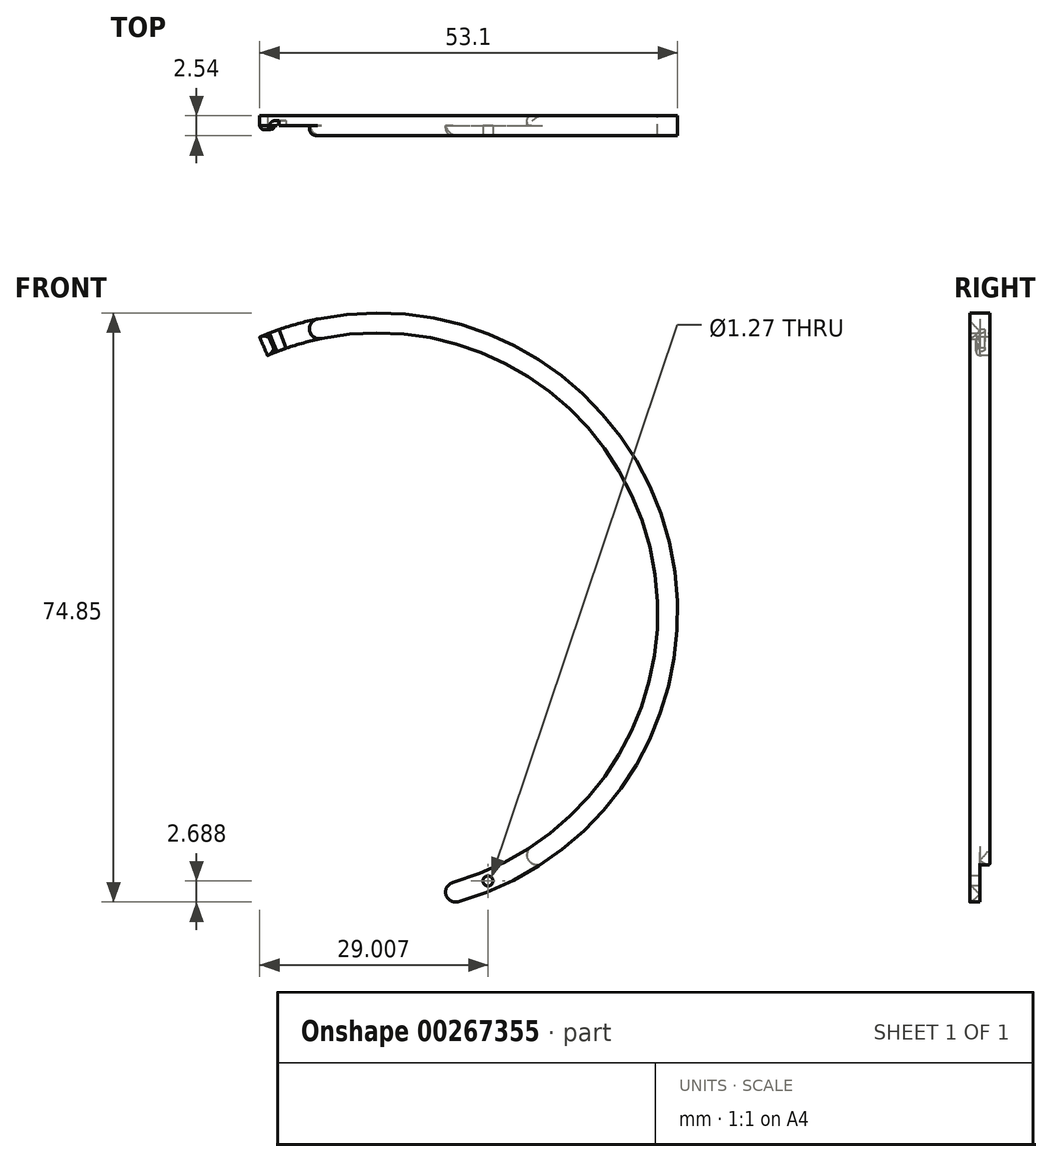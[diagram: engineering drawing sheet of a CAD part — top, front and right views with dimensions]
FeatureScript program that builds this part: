
annotation { "Feature Type Name" : "Feature", "Feature Type Description" : "" }
export const myFeature = defineFeature(function(context is Context, id is Id, definition is map)
    precondition{}
    {
        {
            var Q0;
            Q0=qCreatedBy(makeId("Front.planeOp"),FACE);
            var sketch = newSketch(context, id + "F0", { "sketchPlane" : qUnion([Q0])});
            skArc(sketch, "E0", {"start": v(8.35, -34.57) * mm, "mid": v(34.57, 8.35) * mm, "end": v(-8.35, 34.57) * mm});
            skArc(sketch, "E1", {"start": v(8.95, -37.03) * mm, "mid": v(37.03, 8.95) * mm, "end": v(-8.95, 37.03) * mm});
            skLineSegment(sketch, "E2", {"start": v(-8.95, 37.03) * mm, "end": v(-8.35, 34.57) * mm});
            skLineSegment(sketch, "E3", {"start": v(18.51, -30.36) * mm, "end": v(19.83, -32.53) * mm});
            skLineSegment(sketch, "E4.trimOffspring", {"start": v(8.35, -34.57) * mm, "end": v(8.95, -37.03) * mm});
            skPoint(sketch, "E5", {"position": v(13.43, -32.93) * mm});
            skPoint(sketch, "E6", {"position": v(14.58, -35.2) * mm});
            skLineSegment(sketch, "E7", {"start": v(14.58, -35.2) * mm, "end": v(13.43, -32.93) * mm});
            skArc(sketch, "E8.MirrorCS", {"start": v(8.35, -34.57) * mm, "mid": v(-34.57, -8.35) * mm, "end": v(-8.35, 34.57) * mm});
            skArc(sketch, "E9.MirrorCS", {"start": v(8.95, -37.03) * mm, "mid": v(-37.03, -8.95) * mm, "end": v(-8.95, 37.03) * mm});
            skSolve(sketch);
        }
        {
            var Q0;
            {var subQ0=sQuery(id+"F0.wireOp",EDGE,"E2");Q0=makeQuery(id+"F0.imprint","IMPRINT",FACE,{"disambiguationData":[TD([[makeQuery(id+"F0.imprint","IMPRINT",EDGE,{"derivedFrom":subQ0}),1.0]])]});}
            extrude(context, id + "F1", {"entities" : qUnion([Q0]), "endBound" : BoundingType.SYMMETRIC, "depth" : 2.54 * mm});
        }
        {
            var Q0;
            {var subQ2=sQuery(id+"F0.wireOp",EDGE,"E3");Q0=makeQuery(id+"F0.imprint","IMPRINT",FACE,{"disambiguationData":[TD([[makeQuery(id+"F0.imprint","IMPRINT",EDGE,{"derivedFrom":subQ2}),-1.0]])]});}
            var Q1;
            {var subQ0=sQuery(id+"F0.wireOp",EDGE,"E4.trimOffspring");Q1=makeQuery(id+"F0.imprint","IMPRINT",FACE,{"disambiguationData":[TD([[makeQuery(id+"F0.imprint","IMPRINT",EDGE,{"derivedFrom":subQ0}),1.0]])]});}
            extrude(context, id + "F2", {"entities" : qUnion([Q0, Q1]), "operationType" : NewBodyOperationType.ADD, "depth" : 1.27 * mm});
        }
        {
            var Q0;
            {var subQ0=sQuery(id+"F0.wireOp",EDGE,"E3");var subQ1=sQuery(id+"F0.wireOp",EDGE,"E1");var subQ2=sQuery(id+"F0.wireOp",EDGE,"E0");Q0=makeQuery(id+"F2.boolean.opBoolean","MERGE",FACE,{"derivedFrom":[makeQuery(id+"F1.opExtrude","CAP_FACE",FACE,{"disambiguationData":[OSD([subQ2,subQ1,sQuery(id+"F0.wireOp",EDGE,"E2"),subQ0])],"isStart":false}),makeQuery(id+"F2.opExtrude","CAP_FACE",FACE,{"disambiguationData":[OSD([subQ2,subQ1,subQ0,sQuery(id+"F0.wireOp",EDGE,"E4.trimOffspring")])],"isStart":false})]});}
            var sketch = newSketch(context, id + "F3", { "sketchPlane" : qUnion([Q0])});
            skCircle(sketch, "E10", {"center": v(14, -34.06) * mm, "radius": 0.64 * mm});
            skSolve(sketch);
        }
        {
            var Q0;
            Q0 = qSketchRegion(id + "F3", true);
            extrude(context, id + "F4", {"entities" : qUnion([Q0]), "operationType" : NewBodyOperationType.REMOVE, "endBound" : BoundingType.THROUGH_ALL, "oppositeDirection" : true, "depth" : 25.4 * mm});
        }
        {
            var Q0;
            Q0=makeQuery(id+"F2.opExtrude","CAP_EDGE",EDGE,{"disambiguationData":[OSD([sQuery(id+"F0.wireOp",EDGE,"E4.trimOffspring")])],"isStart":false});
            var Q1;
            Q1=makeQuery(id+"F2.opExtrude","SWEPT_EDGE",EDGE,{"disambiguationData":[OSD([sQuery(id+"F0.wireOp",EDGE,"E0"),sQuery(id+"F0.wireOp",EDGE,"E4.trimOffspring")])]});
            var Q2;
            Q2=makeQuery(id+"F2.opExtrude","SWEPT_EDGE",EDGE,{"disambiguationData":[OSD([sQuery(id+"F0.wireOp",EDGE,"E1"),sQuery(id+"F0.wireOp",EDGE,"E4.trimOffspring")])]});
            var Q3;
            Q3=makeQuery(id+"F1.opExtrude","SWEPT_EDGE",EDGE,{"disambiguationData":[OSD([sQuery(id+"F0.wireOp",EDGE,"E0"),sQuery(id+"F0.wireOp",EDGE,"E3")])]});
            var Q4;
            Q4=makeQuery(id+"F1.opExtrude","SWEPT_EDGE",EDGE,{"disambiguationData":[OSD([sQuery(id+"F0.wireOp",EDGE,"E1"),sQuery(id+"F0.wireOp",EDGE,"E3")])]});
            var Q5;
            Q5=makeQuery(id+"F1.opExtrude","CAP_EDGE",EDGE,{"disambiguationData":[OSD([sQuery(id+"F0.wireOp",EDGE,"E3")])],"isStart":true});
            fillet(context, id + "F5", {"entities" : qUnion([Q0, Q1, Q2, Q3, Q4, Q5]), "radius" : 1.27 * mm, "tangentPropagation" : true, "allowEdgeOverflow" : false});
        }
        {
            var Q0;
            Q0=qCreatedBy(makeId("Front.planeOp"),FACE);
            var sketch = newSketch(context, id + "F6", { "sketchPlane" : qUnion([Q0])});
            skArc(sketch, "E11", {"start": v(-8.35, 34.57) * mm, "mid": v(-11.21, 33.75) * mm, "end": v(-14, 32.7) * mm});
            skArc(sketch, "E12", {"start": v(-8.95, 37.03) * mm, "mid": v(-12.01, 36.16) * mm, "end": v(-15, 35.03) * mm});
            skLineSegment(sketch, "E13", {"start": v(-12.81, 33.17) * mm, "end": v(-13.73, 35.54) * mm});
            skLineSegment(sketch, "E14", {"start": v(-14, 32.7) * mm, "end": v(-15, 35.03) * mm});
            skLineSegment(sketch, "E15", {"start": v(-8.35, 34.57) * mm, "end": v(-8.95, 37.03) * mm});
            skLineSegment(sketch, "E16", {"start": v(-12.54, 35.98) * mm, "end": v(-11.62, 33.6) * mm});
            skSolve(sketch);
        }
        {
            var Q0;
            Q0 = qSketchRegion(id + "F6", true);
            extrude(context, id + "F7", {"entities" : qUnion([Q0]), "operationType" : NewBodyOperationType.ADD, "oppositeDirection" : true, "depth" : 1.27 * mm});
        }
        {
            var Q0;
            {var subQ2=sQuery(id+"F6.wireOp",EDGE,"E13");Q0=makeQuery(id+"F6.imprint","IMPRINT",FACE,{"disambiguationData":[TD([[makeQuery(id+"F6.imprint","IMPRINT",EDGE,{"derivedFrom":subQ2}),1.0]])]});}
            extrude(context, id + "F8", {"entities" : qUnion([Q0]), "operationType" : NewBodyOperationType.ADD, "depth" : 0.64 * mm});
        }
        {
            var Q0;
            Q0=makeQuery(id+"F8.opExtrude","CAP_EDGE",EDGE,{"disambiguationData":[OSD([sQuery(id+"F6.wireOp",EDGE,"E13")])],"isStart":false});
            var Q1;
            Q1=makeQuery(id+"F1.opExtrude","CAP_EDGE",EDGE,{"disambiguationData":[OSD([sQuery(id+"F0.wireOp",EDGE,"E2")])],"isStart":false});
            var Q2;
            Q2=makeQuery(id+"F1.opExtrude","SWEPT_EDGE",EDGE,{"disambiguationData":[OSD([sQuery(id+"F0.wireOp",EDGE,"E1"),sQuery(id+"F0.wireOp",EDGE,"E2"),sQuery(id+"F0.wireOp",EDGE,"E9.MirrorCS")])]});
            var Q3;
            Q3=makeQuery(id+"F1.opExtrude","SWEPT_EDGE",EDGE,{"disambiguationData":[OSD([sQuery(id+"F0.wireOp",EDGE,"E0"),sQuery(id+"F0.wireOp",EDGE,"E2"),sQuery(id+"F0.wireOp",EDGE,"E8.MirrorCS")])]});
            var Q4;
            Q4=makeQuery(id+"F8.opExtrude","SWEPT_EDGE",EDGE,{"disambiguationData":[OSD([sQuery(id+"F6.wireOp",EDGE,"E11"),sQuery(id+"F6.wireOp",EDGE,"E13")])]});
            var Q5;
            Q5=makeQuery(id+"F8.opExtrude","SWEPT_EDGE",EDGE,{"disambiguationData":[OSD([sQuery(id+"F6.wireOp",EDGE,"E12"),sQuery(id+"F6.wireOp",EDGE,"E13")])]});
            fillet(context, id + "F9", {"entities" : qUnion([Q0, Q1, Q2, Q3, Q4, Q5]), "radius" : 1.27 * mm, "tangentPropagation" : true, "allowEdgeOverflow" : false});
        }
        {
            var Q0;
            {var subQ0=sQuery(id+"F6.wireOp",EDGE,"E13");Q0=makeQuery(id+"F6.imprint","IMPRINT",FACE,{"disambiguationData":[TD([[makeQuery(id+"F6.imprint","IMPRINT",EDGE,{"derivedFrom":subQ0}),-1.0]])]});}
            extrude(context, id + "F10", {"entities" : qUnion([Q0]), "operationType" : NewBodyOperationType.REMOVE, "oppositeDirection" : true, "depth" : 0.64 * mm});
        }
        {
            var Q0;
            Q0=makeQuery(id+"F10.boolean.opBoolean","COPY",EDGE,{"derivedFrom":makeQuery(id+"F10.opExtrude","CAP_EDGE",EDGE,{"disambiguationData":[OSD([sQuery(id+"F6.wireOp",EDGE,"E13")])],"isStart":false})});
            var Q1;
            Q1=makeQuery(id+"F8.opExtrude","CAP_EDGE",EDGE,{"disambiguationData":[OSD([sQuery(id+"F6.wireOp",EDGE,"E14")])],"isStart":false});
            fillet(context, id + "F11", {"entities" : qUnion([Q0, Q1]), "radius" : 0.64 * mm, "tangentPropagation" : true, "allowEdgeOverflow" : false});
        }
    });
